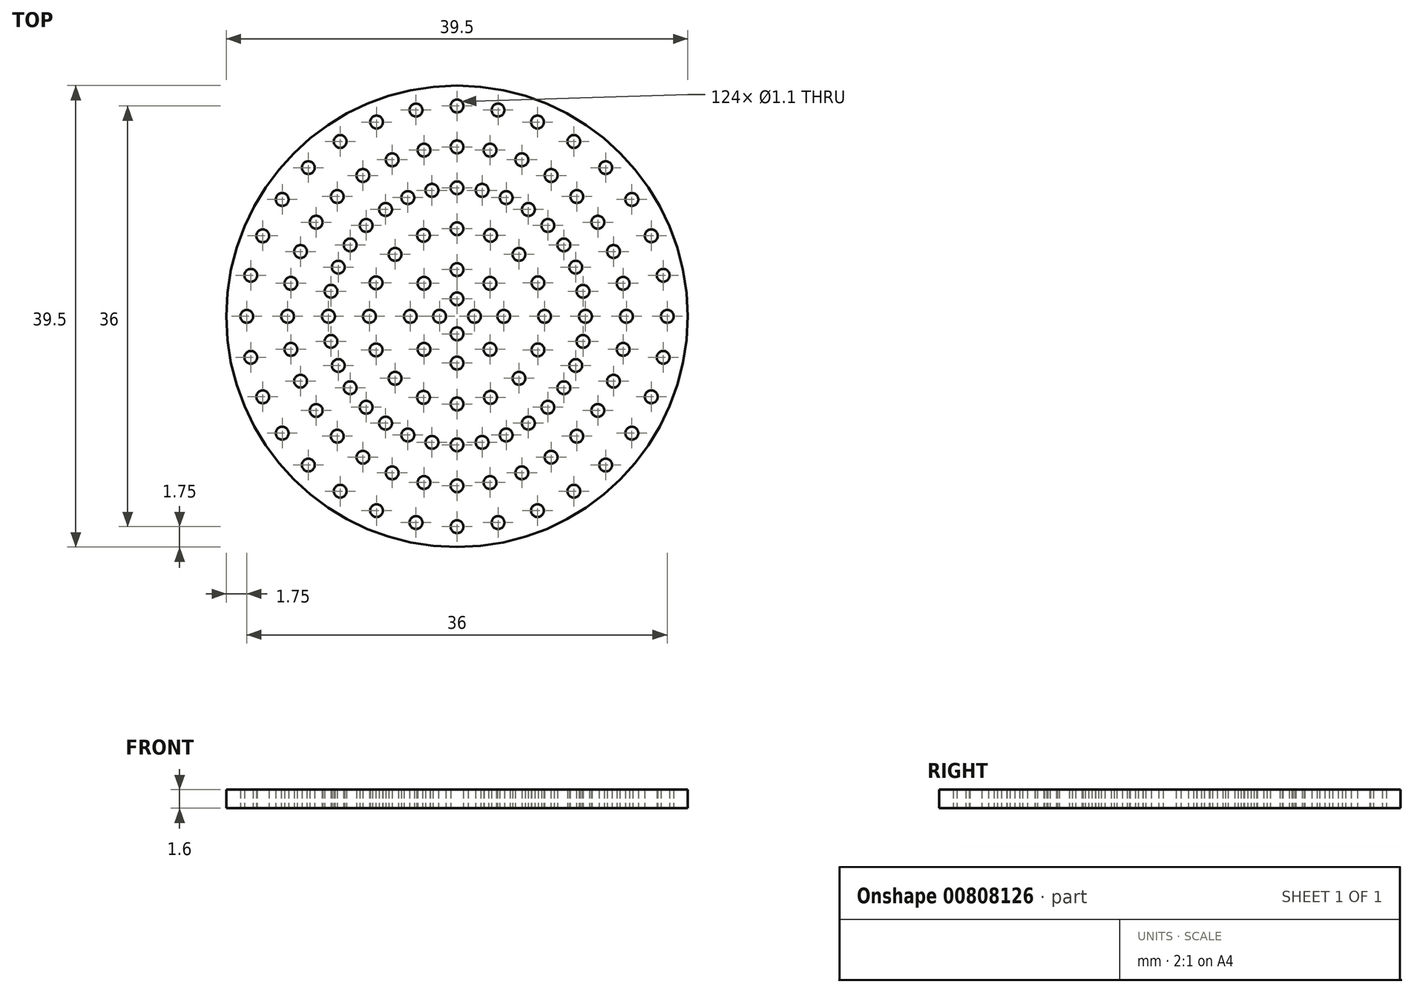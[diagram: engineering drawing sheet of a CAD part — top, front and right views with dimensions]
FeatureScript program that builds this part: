
annotation { "Feature Type Name" : "Feature", "Feature Type Description" : "" }
export const myFeature = defineFeature(function(context is Context, id is Id, definition is map)
    precondition{}
    {
        {
            var Q0;
            Q0=qCreatedBy(makeId("Top.planeOp"),FACE);
            var sketch = newSketch(context, id + "F0", { "sketchPlane" : qUnion([Q0])});
            skCircle(sketch, "E0", {"center": v(0, 0) * mm, "radius": 19.75 * mm});
            skCircle(sketch, "E1", {"center": v(-18, 0) * mm, "radius": 0.55 * mm});
            skCircle(sketch, "E2.1.0", {"center": v(-17.65, -3.51) * mm, "radius": 0.55 * mm});
            skCircle(sketch, "E2.2.0", {"center": v(-16.63, -6.89) * mm, "radius": 0.55 * mm});
            skCircle(sketch, "E2.3.0", {"center": v(-14.97, -10) * mm, "radius": 0.55 * mm});
            skCircle(sketch, "E2.4.0", {"center": v(-12.73, -12.73) * mm, "radius": 0.55 * mm});
            skCircle(sketch, "E2.5.0", {"center": v(-10, -14.97) * mm, "radius": 0.55 * mm});
            skCircle(sketch, "E2.6.0", {"center": v(-6.89, -16.63) * mm, "radius": 0.55 * mm});
            skCircle(sketch, "E2.7.0", {"center": v(-3.51, -17.65) * mm, "radius": 0.55 * mm});
            skCircle(sketch, "E2.8.0", {"center": v(0, -18) * mm, "radius": 0.55 * mm});
            skCircle(sketch, "E2.9.0", {"center": v(3.51, -17.65) * mm, "radius": 0.55 * mm});
            skCircle(sketch, "E2.10.0", {"center": v(6.89, -16.63) * mm, "radius": 0.55 * mm});
            skCircle(sketch, "E2.11.0", {"center": v(10, -14.97) * mm, "radius": 0.55 * mm});
            skCircle(sketch, "E2.12.0", {"center": v(12.73, -12.73) * mm, "radius": 0.55 * mm});
            skCircle(sketch, "E2.13.0", {"center": v(14.97, -10) * mm, "radius": 0.55 * mm});
            skCircle(sketch, "E2.14.0", {"center": v(16.63, -6.89) * mm, "radius": 0.55 * mm});
            skCircle(sketch, "E2.15.0", {"center": v(17.65, -3.51) * mm, "radius": 0.55 * mm});
            skCircle(sketch, "E2.16.0", {"center": v(18, 0) * mm, "radius": 0.55 * mm});
            skCircle(sketch, "E2.17.0", {"center": v(17.65, 3.51) * mm, "radius": 0.55 * mm});
            skCircle(sketch, "E2.18.0", {"center": v(16.63, 6.89) * mm, "radius": 0.55 * mm});
            skCircle(sketch, "E2.19.0", {"center": v(14.97, 10) * mm, "radius": 0.55 * mm});
            skCircle(sketch, "E2.20.0", {"center": v(12.73, 12.73) * mm, "radius": 0.55 * mm});
            skCircle(sketch, "E2.21.0", {"center": v(10, 14.97) * mm, "radius": 0.55 * mm});
            skCircle(sketch, "E2.22.0", {"center": v(6.89, 16.63) * mm, "radius": 0.55 * mm});
            skCircle(sketch, "E2.23.0", {"center": v(3.51, 17.65) * mm, "radius": 0.55 * mm});
            skCircle(sketch, "E2.24.0", {"center": v(0, 18) * mm, "radius": 0.55 * mm});
            skCircle(sketch, "E2.25.0", {"center": v(-3.51, 17.65) * mm, "radius": 0.55 * mm});
            skCircle(sketch, "E2.26.0", {"center": v(-6.89, 16.63) * mm, "radius": 0.55 * mm});
            skCircle(sketch, "E2.27.0", {"center": v(-10, 14.97) * mm, "radius": 0.55 * mm});
            skCircle(sketch, "E2.28.0", {"center": v(-12.73, 12.73) * mm, "radius": 0.55 * mm});
            skCircle(sketch, "E2.29.0", {"center": v(-14.97, 10) * mm, "radius": 0.55 * mm});
            skCircle(sketch, "E2.30.0", {"center": v(-16.63, 6.89) * mm, "radius": 0.55 * mm});
            skCircle(sketch, "E2.31.0", {"center": v(-17.65, 3.51) * mm, "radius": 0.55 * mm});
            skCircle(sketch, "E3", {"center": v(-14.5, 0) * mm, "radius": 0.55 * mm});
            skLineSegment(sketch, "E4.anchor1", {"start": v(0, 0) * mm, "end": v(-14.5, 0) * mm, "construction": true});
            skLineSegment(sketch, "E4.anchor2", {"start": v(0, 0) * mm, "end": v(-14.5, 0) * mm, "construction": true});
            skCircle(sketch, "E5.1.0", {"center": v(-14.22, -2.83) * mm, "radius": 0.55 * mm});
            skCircle(sketch, "E5.2.0", {"center": v(-13.4, -5.55) * mm, "radius": 0.55 * mm});
            skCircle(sketch, "E5.3.0", {"center": v(-12.06, -8.06) * mm, "radius": 0.55 * mm});
            skCircle(sketch, "E5.4.0", {"center": v(-10.25, -10.25) * mm, "radius": 0.55 * mm});
            skCircle(sketch, "E5.5.0", {"center": v(-8.06, -12.06) * mm, "radius": 0.55 * mm});
            skCircle(sketch, "E5.6.0", {"center": v(-5.55, -13.4) * mm, "radius": 0.55 * mm});
            skCircle(sketch, "E5.7.0", {"center": v(-2.83, -14.22) * mm, "radius": 0.55 * mm});
            skCircle(sketch, "E5.8.0", {"center": v(0, -14.5) * mm, "radius": 0.55 * mm});
            skCircle(sketch, "E5.9.0", {"center": v(2.83, -14.22) * mm, "radius": 0.55 * mm});
            skCircle(sketch, "E5.10.0", {"center": v(5.55, -13.4) * mm, "radius": 0.55 * mm});
            skCircle(sketch, "E5.11.0", {"center": v(8.06, -12.06) * mm, "radius": 0.55 * mm});
            skCircle(sketch, "E5.12.0", {"center": v(10.25, -10.25) * mm, "radius": 0.55 * mm});
            skCircle(sketch, "E5.13.0", {"center": v(12.06, -8.06) * mm, "radius": 0.55 * mm});
            skCircle(sketch, "E5.14.0", {"center": v(13.4, -5.55) * mm, "radius": 0.55 * mm});
            skCircle(sketch, "E5.15.0", {"center": v(14.22, -2.83) * mm, "radius": 0.55 * mm});
            skCircle(sketch, "E5.16.0", {"center": v(14.5, 0) * mm, "radius": 0.55 * mm});
            skCircle(sketch, "E5.17.0", {"center": v(14.22, 2.83) * mm, "radius": 0.55 * mm});
            skCircle(sketch, "E5.18.0", {"center": v(13.4, 5.55) * mm, "radius": 0.55 * mm});
            skCircle(sketch, "E5.19.0", {"center": v(12.06, 8.06) * mm, "radius": 0.55 * mm});
            skCircle(sketch, "E5.20.0", {"center": v(10.25, 10.25) * mm, "radius": 0.55 * mm});
            skCircle(sketch, "E5.21.0", {"center": v(8.06, 12.06) * mm, "radius": 0.55 * mm});
            skCircle(sketch, "E5.22.0", {"center": v(5.55, 13.4) * mm, "radius": 0.55 * mm});
            skCircle(sketch, "E5.23.0", {"center": v(2.83, 14.22) * mm, "radius": 0.55 * mm});
            skCircle(sketch, "E5.24.0", {"center": v(0, 14.5) * mm, "radius": 0.55 * mm});
            skCircle(sketch, "E5.25.0", {"center": v(-2.83, 14.22) * mm, "radius": 0.55 * mm});
            skCircle(sketch, "E5.26.0", {"center": v(-5.55, 13.4) * mm, "radius": 0.55 * mm});
            skCircle(sketch, "E5.27.0", {"center": v(-8.06, 12.06) * mm, "radius": 0.55 * mm});
            skCircle(sketch, "E5.28.0", {"center": v(-10.25, 10.25) * mm, "radius": 0.55 * mm});
            skCircle(sketch, "E5.29.0", {"center": v(-12.06, 8.06) * mm, "radius": 0.55 * mm});
            skCircle(sketch, "E5.30.0", {"center": v(-13.4, 5.55) * mm, "radius": 0.55 * mm});
            skCircle(sketch, "E5.31.0", {"center": v(-14.22, 2.83) * mm, "radius": 0.55 * mm});
            skCircle(sketch, "E6", {"center": v(-11, 0) * mm, "radius": 0.55 * mm});
            skCircle(sketch, "E7.1.0", {"center": v(-10.79, -2.15) * mm, "radius": 0.55 * mm});
            skCircle(sketch, "E7.2.0", {"center": v(-10.16, -4.2) * mm, "radius": 0.55 * mm});
            skCircle(sketch, "E7.3.0", {"center": v(-9.15, -6.11) * mm, "radius": 0.55 * mm});
            skCircle(sketch, "E7.4.0", {"center": v(-7.78, -7.78) * mm, "radius": 0.55 * mm});
            skCircle(sketch, "E7.5.0", {"center": v(-6.11, -9.15) * mm, "radius": 0.55 * mm});
            skCircle(sketch, "E7.6.0", {"center": v(-4.2, -10.16) * mm, "radius": 0.55 * mm});
            skCircle(sketch, "E7.7.0", {"center": v(-2.15, -10.79) * mm, "radius": 0.55 * mm});
            skCircle(sketch, "E7.8.0", {"center": v(0, -11) * mm, "radius": 0.55 * mm});
            skCircle(sketch, "E7.9.0", {"center": v(2.15, -10.79) * mm, "radius": 0.55 * mm});
            skCircle(sketch, "E7.10.0", {"center": v(4.2, -10.16) * mm, "radius": 0.55 * mm});
            skCircle(sketch, "E7.11.0", {"center": v(6.11, -9.15) * mm, "radius": 0.55 * mm});
            skCircle(sketch, "E7.12.0", {"center": v(7.78, -7.78) * mm, "radius": 0.55 * mm});
            skCircle(sketch, "E7.13.0", {"center": v(9.15, -6.11) * mm, "radius": 0.55 * mm});
            skCircle(sketch, "E7.14.0", {"center": v(10.16, -4.2) * mm, "radius": 0.55 * mm});
            skCircle(sketch, "E7.15.0", {"center": v(10.79, -2.15) * mm, "radius": 0.55 * mm});
            skCircle(sketch, "E7.16.0", {"center": v(11, 0) * mm, "radius": 0.55 * mm});
            skCircle(sketch, "E7.17.0", {"center": v(10.79, 2.15) * mm, "radius": 0.55 * mm});
            skCircle(sketch, "E7.18.0", {"center": v(10.16, 4.2) * mm, "radius": 0.55 * mm});
            skCircle(sketch, "E7.19.0", {"center": v(9.15, 6.11) * mm, "radius": 0.55 * mm});
            skCircle(sketch, "E7.20.0", {"center": v(7.78, 7.78) * mm, "radius": 0.55 * mm});
            skCircle(sketch, "E7.21.0", {"center": v(6.11, 9.15) * mm, "radius": 0.55 * mm});
            skCircle(sketch, "E7.22.0", {"center": v(4.2, 10.16) * mm, "radius": 0.55 * mm});
            skCircle(sketch, "E7.23.0", {"center": v(2.15, 10.79) * mm, "radius": 0.55 * mm});
            skCircle(sketch, "E7.24.0", {"center": v(0, 11) * mm, "radius": 0.55 * mm});
            skCircle(sketch, "E7.25.0", {"center": v(-2.15, 10.79) * mm, "radius": 0.55 * mm});
            skCircle(sketch, "E7.26.0", {"center": v(-4.2, 10.16) * mm, "radius": 0.55 * mm});
            skCircle(sketch, "E7.27.0", {"center": v(-6.11, 9.15) * mm, "radius": 0.55 * mm});
            skCircle(sketch, "E7.28.0", {"center": v(-7.78, 7.78) * mm, "radius": 0.55 * mm});
            skCircle(sketch, "E7.29.0", {"center": v(-9.15, 6.11) * mm, "radius": 0.55 * mm});
            skCircle(sketch, "E7.30.0", {"center": v(-10.16, 4.2) * mm, "radius": 0.55 * mm});
            skCircle(sketch, "E7.31.0", {"center": v(-10.79, 2.15) * mm, "radius": 0.55 * mm});
            skCircle(sketch, "E8", {"center": v(-7.5, 0) * mm, "radius": 0.55 * mm});
            skCircle(sketch, "E9", {"center": v(-4, 0) * mm, "radius": 0.55 * mm});
            skCircle(sketch, "E10.1.0", {"center": v(-6.93, -2.87) * mm, "radius": 0.55 * mm});
            skCircle(sketch, "E10.2.0", {"center": v(-5.3, -5.3) * mm, "radius": 0.55 * mm});
            skCircle(sketch, "E10.3.0", {"center": v(-2.87, -6.93) * mm, "radius": 0.55 * mm});
            skCircle(sketch, "E10.4.0", {"center": v(0, -7.5) * mm, "radius": 0.55 * mm});
            skCircle(sketch, "E10.5.0", {"center": v(2.87, -6.93) * mm, "radius": 0.55 * mm});
            skCircle(sketch, "E10.6.0", {"center": v(5.3, -5.3) * mm, "radius": 0.55 * mm});
            skCircle(sketch, "E10.7.0", {"center": v(6.93, -2.87) * mm, "radius": 0.55 * mm});
            skCircle(sketch, "E10.8.0", {"center": v(7.5, 0) * mm, "radius": 0.55 * mm});
            skCircle(sketch, "E10.9.0", {"center": v(6.93, 2.87) * mm, "radius": 0.55 * mm});
            skCircle(sketch, "E10.10.0", {"center": v(5.3, 5.3) * mm, "radius": 0.55 * mm});
            skCircle(sketch, "E10.11.0", {"center": v(2.87, 6.93) * mm, "radius": 0.55 * mm});
            skCircle(sketch, "E10.12.0", {"center": v(0, 7.5) * mm, "radius": 0.55 * mm});
            skCircle(sketch, "E10.13.0", {"center": v(-2.87, 6.93) * mm, "radius": 0.55 * mm});
            skCircle(sketch, "E10.14.0", {"center": v(-5.3, 5.3) * mm, "radius": 0.55 * mm});
            skCircle(sketch, "E10.15.0", {"center": v(-6.93, 2.87) * mm, "radius": 0.55 * mm});
            skCircle(sketch, "E11.1.0", {"center": v(-2.83, -2.83) * mm, "radius": 0.55 * mm});
            skCircle(sketch, "E11.2.0", {"center": v(0, -4) * mm, "radius": 0.55 * mm});
            skCircle(sketch, "E11.3.0", {"center": v(2.83, -2.83) * mm, "radius": 0.55 * mm});
            skCircle(sketch, "E11.4.0", {"center": v(4, 0) * mm, "radius": 0.55 * mm});
            skCircle(sketch, "E11.5.0", {"center": v(2.83, 2.83) * mm, "radius": 0.55 * mm});
            skCircle(sketch, "E11.6.0", {"center": v(0, 4) * mm, "radius": 0.55 * mm});
            skCircle(sketch, "E11.7.0", {"center": v(-2.83, 2.83) * mm, "radius": 0.55 * mm});
            skCircle(sketch, "E12", {"center": v(-1.5, 0) * mm, "radius": 0.55 * mm});
            skCircle(sketch, "E13.1.0", {"center": v(0, -1.5) * mm, "radius": 0.55 * mm});
            skCircle(sketch, "E13.2.0", {"center": v(1.5, 0) * mm, "radius": 0.55 * mm});
            skCircle(sketch, "E13.3.0", {"center": v(0, 1.5) * mm, "radius": 0.55 * mm});
            skSolve(sketch);
        }
        {
            var Q0;
            Q0 = qSketchRegion(id + "F0", true);
            extrude(context, id + "F1", {"entities" : qUnion([Q0]), "depth" : 1.6 * mm, "offsetDistance" : 25 * mm});
        }
    });
